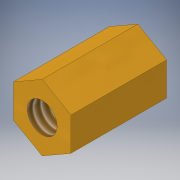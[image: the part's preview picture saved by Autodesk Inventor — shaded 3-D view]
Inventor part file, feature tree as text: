
AUTODESK INVENTOR PART (.ipt)
format: ipt  version: 2019 (Build 230136000, 136)  size: 133,632 bytes
history: native  units: mm
features: other x6, thread x1, extrude x1, hole x1, sketch x1
ambient origin geometry x8: Origin, YZ Plane, XZ Plane, XY Plane, X Axis, Y Axis, Z Axis, Center Point
bodies: Solid1 (feature_tree)
feature tree (10):
  other  "Table"
  thread  "Thread1:Designation = M2x0.4"  [1 undecoded]
  other  "d1 = 5 mm"
  other  "d1 = 10mm"
  other  "d1 = 15mm"
  other  "d1 = 20mm"
  other  "d1 = 25mm"
  extrude  "Hexagon1"  Depth=2.999912mm
  hole  "Hole1"  [1 undecoded]
  sketch  "Sketch1"  dims[d1=5.0mm d2=0.0mm d29=10.0mm d30=10.0mm d5=1.567mm d6=4.0mm d7=4.4mm d8=2.0mm d9=90.0deg d10=4.0mm d11=0.0mm d20=2.999912mm d21=1.732mm]
note: 2 required parameter values undecoded (feature->parameter linkage not recoverable at this tier; creation-order binding heuristic only, values carry confidence <= 0.55)
